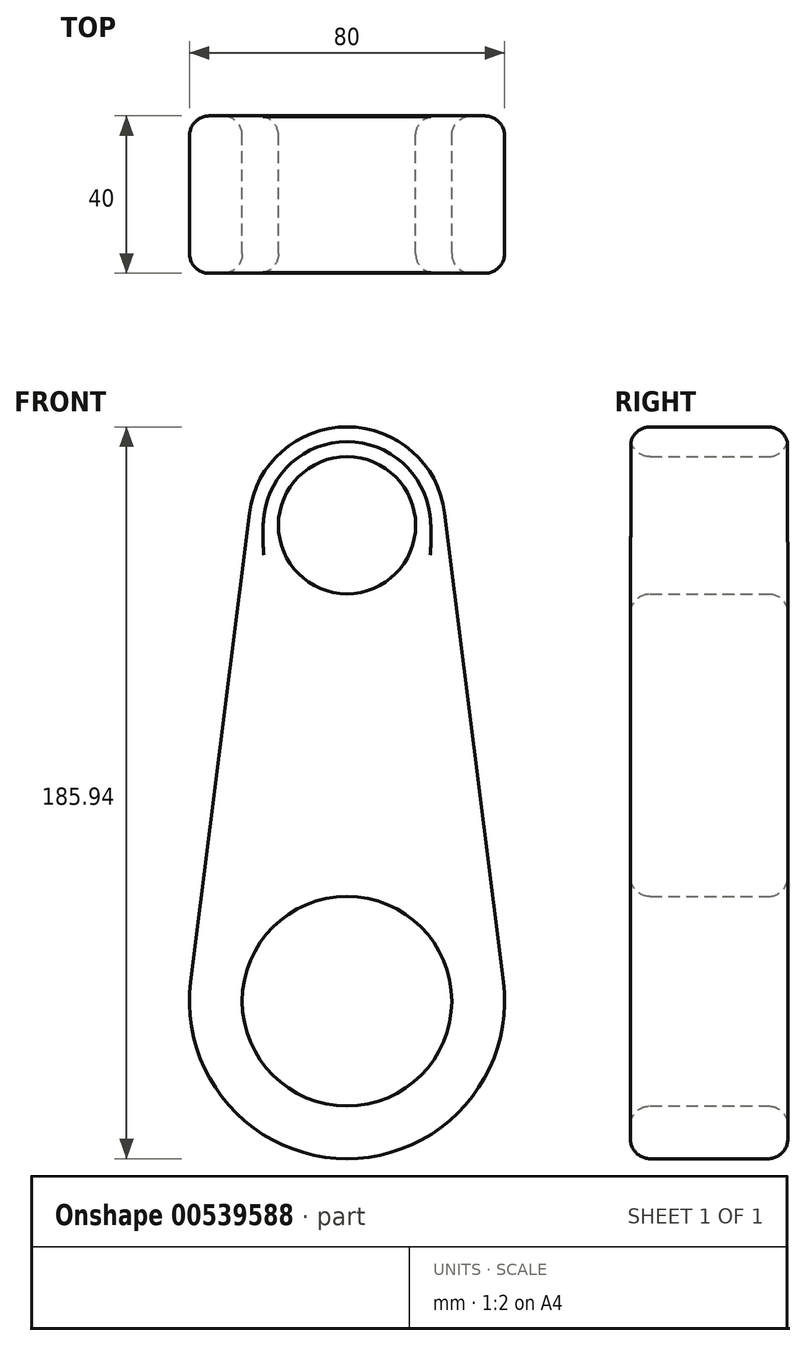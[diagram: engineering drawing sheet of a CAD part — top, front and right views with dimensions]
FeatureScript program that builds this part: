
annotation { "Feature Type Name" : "Feature", "Feature Type Description" : "" }
export const myFeature = defineFeature(function(context is Context, id is Id, definition is map)
    precondition{}
    {
        {
            var Q0;
            Q0=qCreatedBy(makeId("Front.planeOp"),FACE);
            var sketch = newSketch(context, id + "F0", { "sketchPlane" : qUnion([Q0])});
            skCircle(sketch, "E0", {"center": v(0, -20.27) * mm, "radius": 40 * mm});
            skCircle(sketch, "E1", {"center": v(0, 100.67) * mm, "radius": 25 * mm});
            skLineSegment(sketch, "E2", {"start": v(-24.8, 103.77) * mm, "end": v(-39.7, -15.3) * mm});
            skLineSegment(sketch, "E3", {"start": v(24.8, 103.77) * mm, "end": v(39.7, -15.3) * mm});
            skCircle(sketch, "E4", {"center": v(0, 100.67) * mm, "radius": 17.43 * mm});
            skCircle(sketch, "E5", {"center": v(0, -20.27) * mm, "radius": 26.62 * mm});
            skSolve(sketch);
        }
        {
            var Q0;
            Q0=makeQuery(id+"F0.imprint","IMPRINT",FACE,{"disambiguationData":[TD([[makeQuery(id+"F0.imprint","IMPRINT",EDGE,{"derivedFrom":sQuery(id+"F0.wireOp",EDGE,"E5")}),-1.0]])]});
            var Q1;
            {var subQ0=sQuery(id+"F0.wireOp",EDGE,"E2");Q1=makeQuery(id+"F0.imprint","IMPRINT",FACE,{"disambiguationData":[TD([[makeQuery(id+"F0.imprint","IMPRINT",EDGE,{"derivedFrom":subQ0}),1.0]])]});}
            var Q2;
            Q2=makeQuery(id+"F0.imprint","IMPRINT",FACE,{"disambiguationData":[TD([[makeQuery(id+"F0.imprint","IMPRINT",EDGE,{"derivedFrom":sQuery(id+"F0.wireOp",EDGE,"E4")}),-1.0]])]});
            extrude(context, id + "F1", {"entities" : qUnion([Q0, Q1, Q2]), "depth" : 40 * mm, "offsetDistance" : 25 * mm});
        }
        {
            var Q0;
            Q0=makeQuery(id+"F1.opExtrude","CAP_EDGE",EDGE,{"disambiguationData":[OSD([sQuery(id+"F0.wireOp",EDGE,"E4")])],"isStart":false});
            var Q1;
            Q1=makeQuery(id+"F1.opExtrude","CAP_EDGE",EDGE,{"disambiguationData":[OSD([sQuery(id+"F0.wireOp",EDGE,"E5")])],"isStart":false});
            var Q2;
            Q2=makeQuery(id+"F1.opExtrude","CAP_EDGE",EDGE,{"disambiguationData":[OSD([sQuery(id+"F0.wireOp",EDGE,"E5")])],"isStart":true});
            var Q3;
            Q3=makeQuery(id+"F1.opExtrude","CAP_EDGE",EDGE,{"disambiguationData":[OSD([sQuery(id+"F0.wireOp",EDGE,"E4")])],"isStart":true});
            var Q4;
            Q4=makeQuery(id+"F1.opExtrude","CAP_EDGE",EDGE,{"disambiguationData":[OSD([sQuery(id+"F0.wireOp",EDGE,"E3")])],"isStart":true});
            var Q5;
            Q5=makeQuery(id+"F1.opExtrude","CAP_EDGE",EDGE,{"disambiguationData":[OSD([sQuery(id+"F0.wireOp",EDGE,"E1")])],"isStart":true});
            var Q6;
            Q6=makeQuery(id+"F1.opExtrude","CAP_EDGE",EDGE,{"disambiguationData":[OSD([sQuery(id+"F0.wireOp",EDGE,"E3")])],"isStart":false});
            var Q7;
            Q7=makeQuery(id+"F1.opExtrude","CAP_EDGE",EDGE,{"disambiguationData":[OSD([sQuery(id+"F0.wireOp",EDGE,"E2")])],"isStart":false});
            fillet(context, id + "F2", {"entities" : qUnion([Q0, Q1, Q2, Q3, Q4, Q5, Q6, Q7]), "radius" : 5 * mm, "tangentPropagation" : true, "allowEdgeOverflow" : false});
        }
    });
